# Revit family: EKF_EE_ДержательDIN-реек(10 шт)Trivia_AVERES
name_source: partatom
category: Электрооборудование
units: mm (PartAtom-declared; Revit-internal decimal feet)

## family parameters
Всегда вертикально = Нет
На основе рабочей плоскости = Да
Общий = Да
При загрузке вырезать с полостями = Нет
Размер круглого соединителя = Использовать диаметр
Тип детали = Силовой щит
Точка расчета площади = Нет

## types (2) — shared parameters
ADSK_Единица измерения = шт.
ADSK_Завод-изготовитель = EKF
ADSK_Количество = 1
ADSK_Размер_Глубина = 1.5 мм
ADSK_Размер_Ширина = 165 мм
t1 = 1.5 мм
Изготовитель = EKF
Отметка по умолчанию = 1219.2 мм
ОтступКрайнихОтверстий = 12 мм
Серия номенклатуры = Averes
Степень защиты IP = -
ТВ = EKF_2_TRIVIA_AVERES
Тип установки = -
Ширина = 165 мм
zero-valued in all types: ADSK_Масса

## per-type parameters (varying)
| type | ADSK_Код изделия | ADSK_Марка | ADSK_Наименование | ADSK_Обозначение | ADSK_Размер_Высота | Высота | Количество | Тип |
| Держатель DIN-реек 3-канала (10шт) EKF AVERES | ADH3 | Держатель DIN-реек 3-канала (10 шт) EKF AVERES | Держатель DIN-реек 3-канала (10 шт) EKF AVERES | Держатель DIN-реек 3-канала (10 шт) EKF AVERES | 74.5 мм | 74.5 мм | 3 | 645 мм |
| Держатель DIN-реек 6-каналов (10шт) EKF AVERES | ADH6 | Держатель DIN-реек 6-каналов (10 шт) EKF AVERES | Держатель DIN-реек 6-каналов (10 шт) EKF AVERES | Держатель DIN-реек 6-каналов (10 шт) EKF AVERES | 149 мм | 149 мм | 6 | 646 мм |
